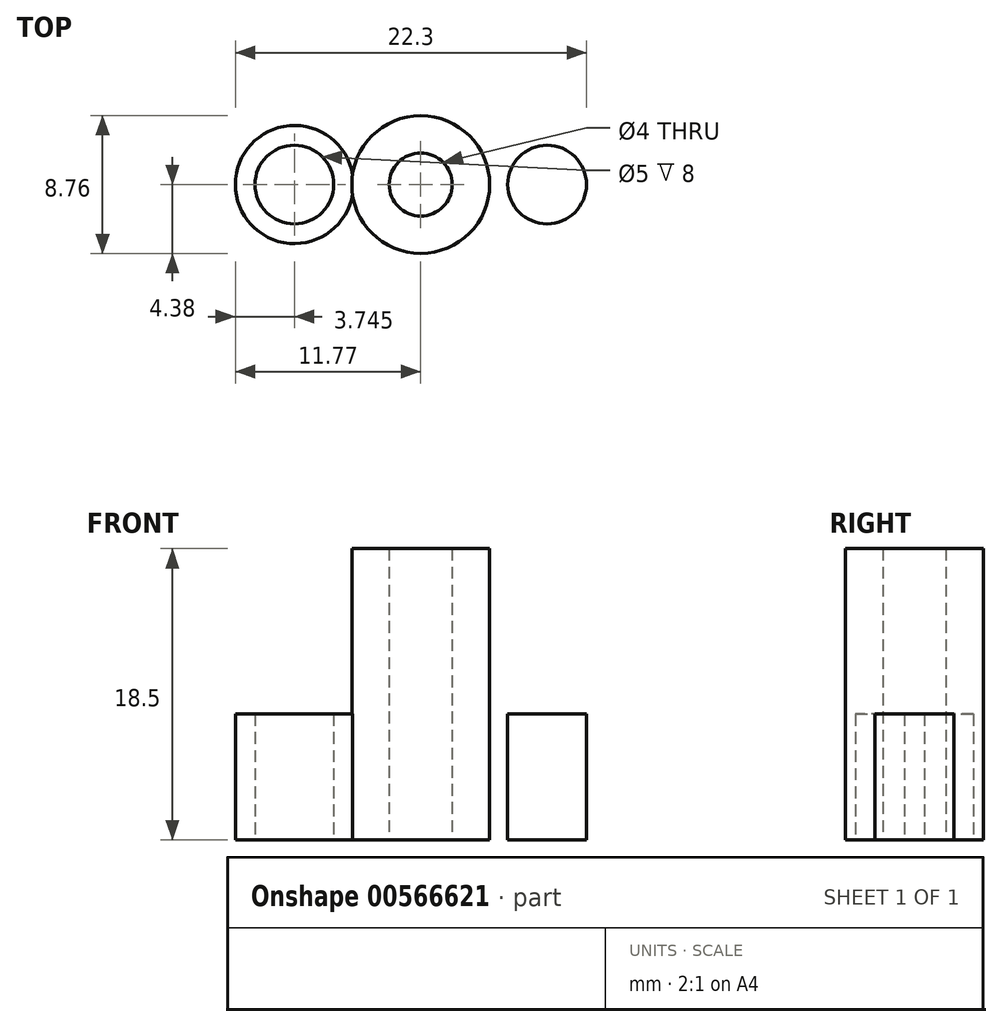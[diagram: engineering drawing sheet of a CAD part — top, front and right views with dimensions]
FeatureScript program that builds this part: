
annotation { "Feature Type Name" : "Feature", "Feature Type Description" : "" }
export const myFeature = defineFeature(function(context is Context, id is Id, definition is map)
    precondition{}
    {
        {
            var Q0;
            Q0=qCreatedBy(makeId("Front.planeOp"),FACE);
            var sketch = newSketch(context, id + "F0", { "sketchPlane" : qUnion([Q0])});
            skLineSegment(sketch, "E0.bottom", {"start": v(0, 0) * mm, "end": v(-4.37, 0) * mm});
            skLineSegment(sketch, "E0.top", {"start": v(-2, 18.5) * mm, "end": v(-4.38, 18.5) * mm});
            skLineSegment(sketch, "E0.left", {"start": v(0, 0) * mm, "end": v(0, 18.5) * mm});
            skLineSegment(sketch, "E0.right", {"start": v(-4.37, 2) * mm, "end": v(-4.38, 18.5) * mm});
            skLineSegment(sketch, "E1.bottom", {"start": v(-2, 0) * mm, "end": v(-13.84, 0) * mm});
            skLineSegment(sketch, "E1.top", {"start": v(-4.37, 2) * mm, "end": v(-13.84, 2) * mm});
            skLineSegment(sketch, "E1.left", {"start": v(0, 0) * mm, "end": v(0, 2) * mm});
            skLineSegment(sketch, "E1.right", {"start": v(-13.84, 0) * mm, "end": v(-13.84, 2) * mm});
            skLineSegment(sketch, "E2.0", {"start": v(-2, 0) * mm, "end": v(-2, 18.5) * mm});
            skSolve(sketch);
        }
        {
            var Q0;
            Q0=makeQuery(id+"F0.imprint","IMPRINT",FACE,{"disambiguationData":[TD([[makeQuery(id+"F0.imprint","IMPRINT",EDGE,{"derivedFrom":sQuery(id+"F0.wireOp",EDGE,"E0.top")}),1.0]])]});
            var Q1;
            Q1=sQuery(id+"F0.wireOp",EDGE,"E0.left");
            revolve(context, id + "F1", {"entities" : qUnion([Q0]), "axis" : qUnion([Q1]), "revolveType" : RevolveType.FULL});
        }
        {
            var Q0;
            Q0=makeQuery(id+"F1.opRevolve","SWEPT_FACE",FACE,{"disambiguationData":[OSD([sQuery(id+"F0.wireOp",EDGE,"E1.top")])]});
            var sketch = newSketch(context, id + "F2", { "sketchPlane" : qUnion([Q0])});
            skCircle(sketch, "E3", {"center": v(-8.02, 0) * mm, "radius": 3.75 * mm});
            skCircle(sketch, "E4", {"center": v(-8.02, 0) * mm, "radius": 2.5 * mm});
            skCircle(sketch, "E5.MirrorC", {"center": v(8.02, 0) * mm, "radius": 2.5 * mm});
            skCircle(sketch, "E6.MirrorC", {"center": v(8.02, 0) * mm, "radius": 3.75 * mm});
            skSolve(sketch);
        }
        {
            var Q0;
            Q0=makeQuery(id+"F2.imprint","IMPRINT",FACE,{"disambiguationData":[TD([[makeQuery(id+"F2.imprint","IMPRINT",EDGE,{"derivedFrom":sQuery(id+"F2.wireOp",EDGE,"E4")}),-1.0]])]});
            var Q1;
            Q1=makeQuery(id+"F2.imprint","IMPRINT",FACE,{"disambiguationData":[TD([[makeQuery(id+"F2.imprint","IMPRINT",EDGE,{"derivedFrom":sQuery(id+"F2.wireOp",EDGE,"E5.MirrorC")}),1.0]])]});
            extrude(context, id + "F3", {"entities" : qUnion([Q0, Q1]), "operationType" : NewBodyOperationType.ADD, "depth" : 6 * mm, "offsetDistance" : 25 * mm});
        }
        {
            var Q0;
            Q0=makeQuery(id+"F3.boolean.opBoolean","SPLIT",FACE,{"disambiguationData":[TD([makeQuery(id+"F3.opExtrude","SWEPT_FACE",FACE,{"disambiguationData":[OSD([sQuery(id+"F2.wireOp",EDGE,"E4")])]})])],"derivedFrom":makeQuery(id+"F1.opRevolve","SWEPT_FACE",FACE,{"disambiguationData":[OSD([sQuery(id+"F0.wireOp",EDGE,"E1.top")])]})});
            var Q1;
            Q1=makeQuery(id+"F3.boolean.opBoolean","SPLIT",FACE,{"disambiguationData":[TD([makeQuery(id+"F3.opExtrude","SWEPT_FACE",FACE,{"disambiguationData":[OSD([sQuery(id+"F2.wireOp",EDGE,"E5.MirrorC")])]})])],"derivedFrom":makeQuery(id+"F1.opRevolve","SWEPT_FACE",FACE,{"disambiguationData":[OSD([sQuery(id+"F0.wireOp",EDGE,"E1.top")])]})});
            extrude(context, id + "F4", {"entities" : qUnion([Q0, Q1]), "operationType" : NewBodyOperationType.REMOVE, "oppositeDirection" : true, "depth" : 25 * mm, "offsetDistance" : 25 * mm});
        }
    });
